# Revit family: KB301 Series
name_source: partatom
category: Plumbing Fixtures
units: mm (PartAtom-declared; Revit-internal decimal feet)

## family parameters
Always vertical = No
Cut with Voids When Loaded = No
Part Type = Normal
Room Calculation Point = No
Round Connector Dimension = Use Diameter
Shared = Yes
Work Plane-Based = No

## types (6) — shared parameters
CW Connection = Yes
Description = Surface-Mounted Baby Changing Station - Vertical
Finish - Hook = Stainless Steel-Koala Kare-Polished
HW Connection = Yes
Manufacturer = Koala Kare
Modified Issue = 20220214.01
Vent Connection = Yes
Waste Connection = Yes

## per-type parameters (varying)
| type | Closed | Materials and Finishes | Open |
| KB301-00-Open | No | Polypropylene-Koala Kare-Beige | Yes |
| KB301-01-Open | No | Polypropylene-Koala Kare-Grey | Yes |
| KB301-05-Open | No | Polypropylene-Koala Kare-White Granite | Yes |
| KB301-00-Closed | Yes | Polypropylene-Koala Kare-Beige | No |
| KB301-01-Closed | Yes | Polypropylene-Koala Kare-Grey | No |
| KB301-05-Closed | Yes | Polypropylene-Koala Kare-White Granite | No |

note: column(s) folded — value = type name in every type: Model

## geometry (parser evidence)
native form markers: Blend x45, Sweep x7
no freeform markers — native parametric forms only
